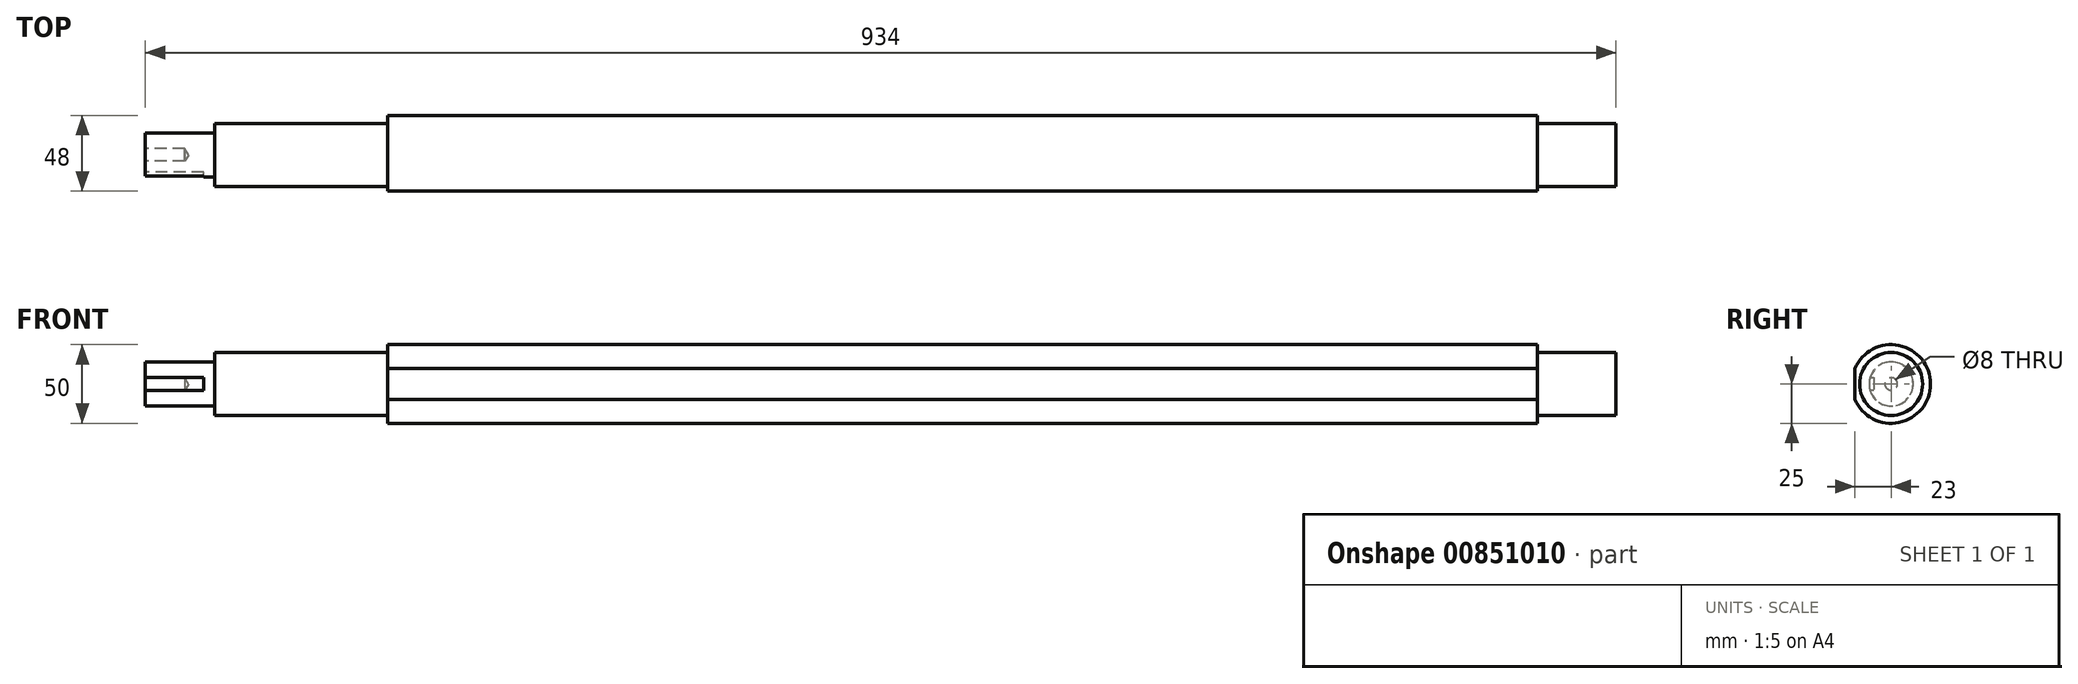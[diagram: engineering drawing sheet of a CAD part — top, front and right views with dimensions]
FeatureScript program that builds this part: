
annotation { "Feature Type Name" : "Feature", "Feature Type Description" : "" }
export const myFeature = defineFeature(function(context is Context, id is Id, definition is map)
    precondition{}
    {
        {
            var Q0;
            Q0=qCreatedBy(makeId("Front.planeOp"),FACE);
            var sketch = newSketch(context, id + "F0", { "sketchPlane" : qUnion([Q0])});
            skLineSegment(sketch, "E0", {"start": v(0, 0) * mm, "end": v(934, 0) * mm});
            skLineSegment(sketch, "E1", {"start": v(934, 0) * mm, "end": v(934, -20) * mm});
            skLineSegment(sketch, "E2", {"start": v(934, -20) * mm, "end": v(884, -20) * mm});
            skLineSegment(sketch, "E3", {"start": v(884, -20) * mm, "end": v(884, -25) * mm});
            skLineSegment(sketch, "E4", {"start": v(884, -25) * mm, "end": v(154, -25) * mm});
            skLineSegment(sketch, "E5", {"start": v(154, -25) * mm, "end": v(154, -20) * mm});
            skLineSegment(sketch, "E6", {"start": v(154, -20) * mm, "end": v(44, -20) * mm});
            skLineSegment(sketch, "E7", {"start": v(0, -14) * mm, "end": v(0, 0) * mm});
            skLineSegment(sketch, "E8", {"start": v(0, -14) * mm, "end": v(44, -14) * mm});
            skLineSegment(sketch, "E9", {"start": v(44, -14) * mm, "end": v(44, -20) * mm});
            skSolve(sketch);
        }
        {
            var Q0;
            Q0=makeQuery(id+"F0.imprint","IMPRINT",FACE,{"disambiguationData":[TD([[makeQuery(id+"F0.imprint","IMPRINT",EDGE,{"derivedFrom":sQuery(id+"F0.wireOp",EDGE,"E0")}),-1.0]])]});
            var Q1;
            Q1=sQuery(id+"F0.wireOp",EDGE,"E0");
            revolve(context, id + "F1", {"surfaceOperationType" : NewSurfaceOperationType.NEW, "entities" : qUnion([Q0]), "axis" : qUnion([Q1]), "revolveType" : RevolveType.FULL});
        }
        {
            var Q0;
            Q0=makeQuery(id+"F1.opRevolve","SWEPT_FACE",FACE,{"disambiguationData":[OSD([sQuery(id+"F0.wireOp",EDGE,"E7")])]});
            var sketch = newSketch(context, id + "F2", { "sketchPlane" : qUnion([Q0])});
            skLineSegment(sketch, "E10", {"start": v(11, 4) * mm, "end": v(11, -4) * mm});
            skLineSegment(sketch, "E11", {"start": v(11, -4) * mm, "end": v(15, -4) * mm});
            skLineSegment(sketch, "E12", {"start": v(15, -4) * mm, "end": v(15, 4) * mm});
            skLineSegment(sketch, "E13", {"start": v(15, 4) * mm, "end": v(11, 4) * mm});
            skPoint(sketch, "E14", {"position": v(0, 0) * mm});
            skSolve(sketch);
        }
        {
            var Q0;
            Q0 = qSketchRegion(id + "F2", true);
            extrude(context, id + "F3", {"entities" : qUnion([Q0]), "operationType" : NewBodyOperationType.REMOVE, "oppositeDirection" : true, "depth" : 37 * mm, "offsetDistance" : 25 * mm});
        }
        {
            var Q0;
            Q0=makeQuery(id+"F1.opRevolve","SWEPT_FACE",FACE,{"disambiguationData":[OSD([sQuery(id+"F0.wireOp",EDGE,"E5")])]});
            var sketch = newSketch(context, id + "F4", { "sketchPlane" : qUnion([Q0])});
            skLineSegment(sketch, "E15.bottom", {"start": v(44.7, 41.67) * mm, "end": v(23, 41.67) * mm});
            skLineSegment(sketch, "E15.top", {"start": v(44.7, -42.14) * mm, "end": v(23, -42.14) * mm});
            skLineSegment(sketch, "E15.left", {"start": v(44.7, 41.67) * mm, "end": v(44.7, -42.14) * mm});
            skLineSegment(sketch, "E15.right", {"start": v(23, 41.67) * mm, "end": v(23, -42.14) * mm});
            skSolve(sketch);
        }
        {
            var Q0;
            Q0 = qSketchRegion(id + "F4", true);
            extrude(context, id + "F5", {"entities" : qUnion([Q0]), "operationType" : NewBodyOperationType.REMOVE, "oppositeDirection" : true, "depth" : 752 * mm, "offsetDistance" : 25 * mm});
        }
        {
            var Q0;
            Q0=sQuery(id+"F2.wireOp",VERTEX,"E14");
            var Q1;
            Q1=makeQuery(id+"F1.opRevolve","SWEPT_BODY",BODY,{"disambiguationData":[OSD([sQuery(id+"F0.wireOp",EDGE,"E0"),sQuery(id+"F0.wireOp",EDGE,"E1"),sQuery(id+"F0.wireOp",EDGE,"E2"),sQuery(id+"F0.wireOp",EDGE,"E3"),sQuery(id+"F0.wireOp",EDGE,"E4"),sQuery(id+"F0.wireOp",EDGE,"E5"),sQuery(id+"F0.wireOp",EDGE,"E6"),sQuery(id+"F0.wireOp",EDGE,"E7"),sQuery(id+"F0.wireOp",EDGE,"E8"),sQuery(id+"F0.wireOp",EDGE,"E9")])]});
            hole(context, id + "F6", {"style" : HoleStyle.SIMPLE, "endStyle" : HoleEndStyle.BLIND, "holeDiameter" : 8 * mm, "majorDiameter" : 5 * mm, "holeDepth" : 25 * mm, "isTappedThrough" : true, "tappedDepth" : 12 * mm, "tapClearance" : 3, "locations" : qUnion([Q0]), "scope" : qUnion([Q1])});
        }
    });
